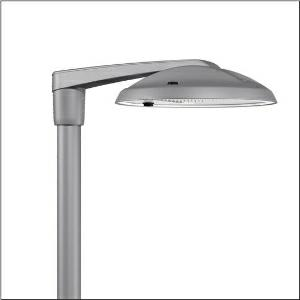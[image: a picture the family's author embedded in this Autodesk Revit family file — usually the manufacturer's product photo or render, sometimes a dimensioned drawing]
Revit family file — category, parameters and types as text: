
# Revit family: dl_50_iq_mini___st1_0a_5xa248d31y08le_1420
name_source: partatom
category: Lighting Fixtures
units: mm (PartAtom-declared; Revit-internal decimal feet)

## family parameters
Cut with Voids When Loaded = No
Host = Face
Light Source = No
Part Type = Normal
Room Calculation Point = No
Round Connector Dimension = Use Diameter
Shared = No

## types (1)
- --- (1 x LED, 10390 lm, 66 W, 3000K)
    Apparent Load = 66 VA
    CIE Flux Codes = 37 72 97 100 100
    Color Rendering = 70
    Color Temperature = 3000K
    Default Elevation = 1800 mm
    Description = DL 50 iQ mini, mast luminaire, primary light control with lens, of PMMA, primary optical cover: cover, of toughened safety glass, transparent, light distribution: ST1.0a, light emission: direct distribution, primary light characteristic: asymmetric, installation type: post-top, side-entry, LED, High Power LED, rated luminous flux: 10.390lm, luminous efficacy: 157lm/W, light colour: 730, colour temperature: 3000K, control gear: iQ-Street Remote, D4i with power reduction, control: optimised constant luminous flux control (CLO 2.0), Desk-Remote (wireless, voltage-free reading and setting of iQ features in the workshop via application-optimized NFC function/RFID function), Light-Fading, Smart-Wire, Night-Set, Lumen-Switch, Temp-Guard, Auto-Match, Street-Remote, pre-setting: logarithmic dimming characteristic, mains connection: 230..240V, AC, 50/60Hz, connection cable pre-assembled, cable length: 8,5m, start of lifetime: 66W, end of service life: 69W, reduction: 30W, luminaire housing, of diecast aluminium, powder-coated, SITECO metallic grey (DB 702S), inclination adjustable: 0°, 5°, 10° (post-top) | 0°, -5°, -10°, -15° (side-entry), please order mast post-top element or mast side-entry element separately, diameter: 500mm, height: 115mm, post-top: for spigot size d x l = 76 x 100mm; with reducer (optional accessory) 60 x 100mm | side-entry: for spigot size d x l = 60 x 100mm; with reducer (optional accessory) 42 x 100mm, mounting height: 4..6m, Smart Interface below and above, protection rating (complete): IP66, insulation class (complete): insulation class II (safety insulation), certification: CE, ENEC, ENEC+, VDE, impact resistance: IK08, permissible operating ambient temperature for outdoor applications: -25..+40°C, standard-compliant lighting for roads and squares, packaging unit: 1 piece

Light Distribution: ST1.0a
    Height = 115 mm
    Lamp = 1 x LED
    Lamp Light Flux = 10390 lm
    Lamp Power = 66 W
    Lamp count = 1
    Length = 500 mm
    Luminous efficacy = 157 lm/W
    Manufacturer = Siteco
    ModVariant = No
    Model = 5XA248D31Y08LE
    Number of Poles = 1
    OnlyDefault = Yes
    Power Factor = 1
    Product Name = DL 50 iQ mini | ST1.0a
    Product group = mast luminaire | pylon top
    ProductGroupID = 6100
    Protection Class = Protection class II
    Protection Degree = IP 66
    RLX_Detail_Level = 1
    RLX_Emergency_Light_Flux = 0 lm
    RLX_Emergency_Type = 0
    RLX_Emergency_Type_DB = No
    RlxData = <blob elided: 107081 chars, md5=65a2750f>
    Socket = socket
    Standby Power = 0 W
    System Light Flux = 10390 lm
    System Power = 66 W
    Type Comments = factory setting: luminous flux: 100 % | dim-lin: 254 | 691 mA
    Type Image = l_1251786.jpg
    URL = http://relux.com
    VarID = @adj_073091
    Voltage = 0 V
    Weight = 0.00 kg
    Width = 0 mm  [stored 0 ft]

note: [stored X ft] marks values corroborated as IEEE doubles in the binary element streams (Revit-internal decimal feet)

## geometry (parser evidence)
native form markers: Blend x4, Sweep x8
no freeform markers — native parametric forms only
